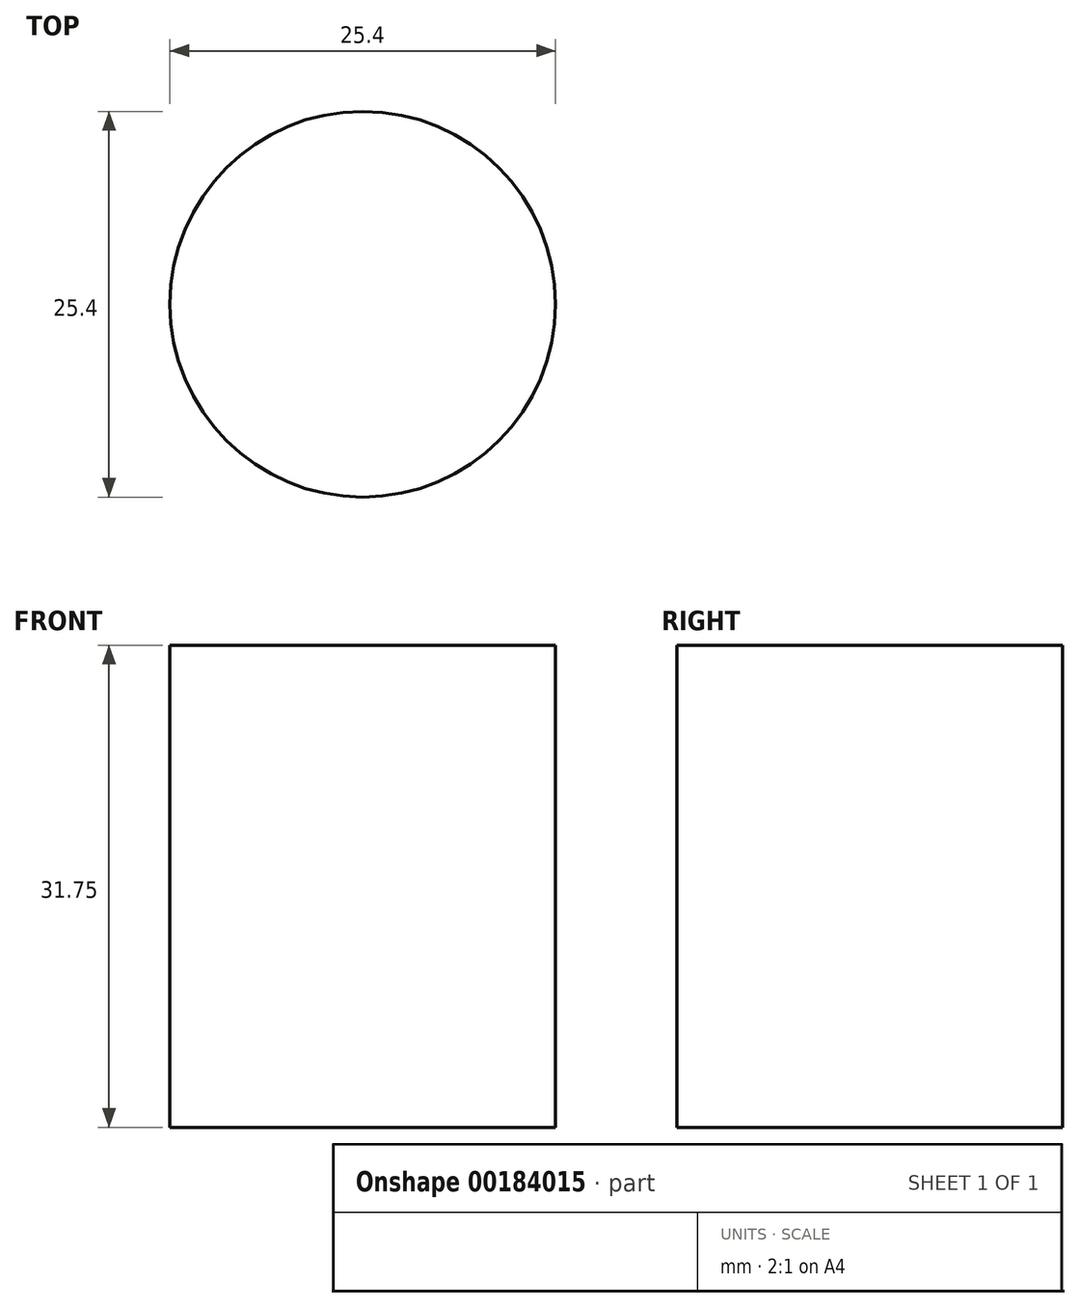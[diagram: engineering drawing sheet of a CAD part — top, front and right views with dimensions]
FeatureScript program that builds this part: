
annotation { "Feature Type Name" : "Feature", "Feature Type Description" : "" }
export const myFeature = defineFeature(function(context is Context, id is Id, definition is map)
    precondition{}
    {
        {
            var Q0;
            Q0=qCreatedBy(makeId("Top.planeOp"),FACE);
            var sketch = newSketch(context, id + "F0", { "sketchPlane" : qUnion([Q0])});
            skCircle(sketch, "E0", {"center": v(0, 0) * mm, "radius": 12.7 * mm});
            skSolve(sketch);
        }
        {
            var Q0;
            Q0 = qSketchRegion(id + "F0", true);
            extrude(context, id + "F1", {"entities" : qUnion([Q0]), "depth" : 31.75 * mm});
        }
        {
            var Q0;
            Q0=makeQuery(id+"F1.opExtrude","CAP_FACE",FACE,{"disambiguationData":[OSD([sQuery(id+"F0.wireOp",EDGE,"E0")])],"isStart":false});
            var sketch = newSketch(context, id + "F2", { "sketchPlane" : qUnion([Q0])});
            skCircle(sketch, "E1", {"center": v(0, 0) * mm, "radius": 4 * mm});
            skSolve(sketch);
        }
        {
            var Q0;
            Q0=sQuery(id+"F2.wireOp",EDGE,"E1");
            extrude(context, id + "F3", {"bodyType" : ToolBodyType.SURFACE, "surfaceEntities" : qUnion([Q0]), "depth" : 16 * mm});
        }
    });
